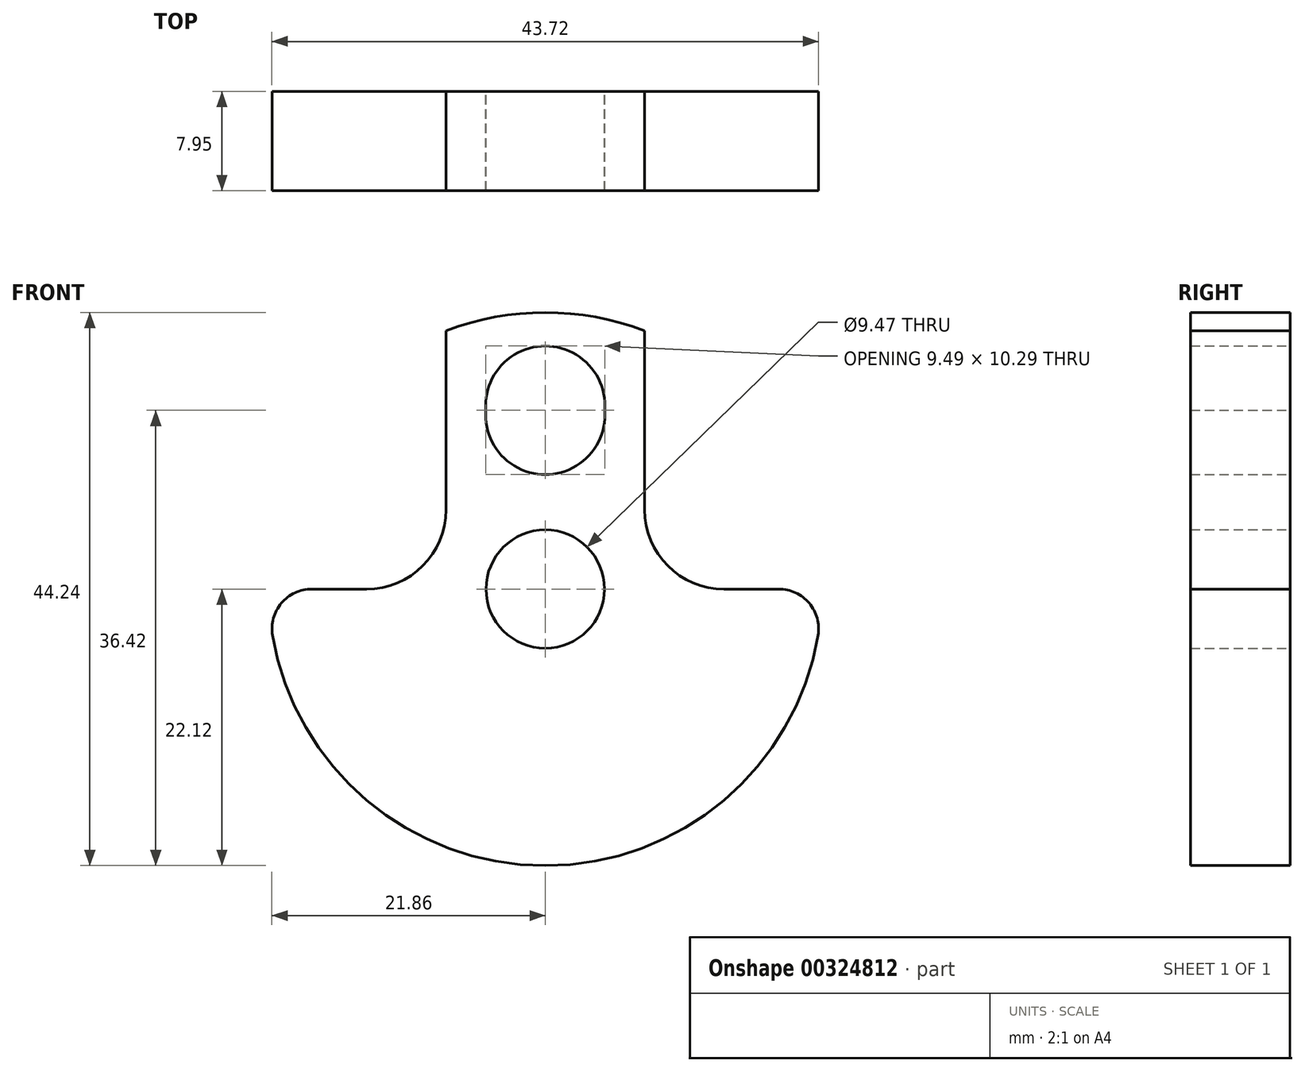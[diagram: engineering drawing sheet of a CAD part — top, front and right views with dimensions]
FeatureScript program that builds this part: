
annotation { "Feature Type Name" : "Feature", "Feature Type Description" : "" }
export const myFeature = defineFeature(function(context is Context, id is Id, definition is map)
    precondition{}
    {
        {
            var Q0;
            Q0=qCreatedBy(makeId("Front.planeOp"),FACE);
            var sketch = newSketch(context, id + "F0", { "sketchPlane" : qUnion([Q0])});
            skArc(sketch, "E0", {"start": v(-22.12, 0) * mm, "mid": v(0, -22.12) * mm, "end": v(22.12, 0) * mm});
            skCircle(sketch, "E1", {"center": v(0, 0) * mm, "radius": 4.74 * mm});
            skLineSegment(sketch, "E2", {"start": v(-7.94, 0) * mm, "end": v(-7.94, 20.65) * mm});
            skLineSegment(sketch, "E3.MirrorCS", {"start": v(7.94, 0) * mm, "end": v(7.94, 20.65) * mm});
            skLineSegment(sketch, "E4", {"start": v(-7.94, 0) * mm, "end": v(-22.12, 0) * mm});
            skLineSegment(sketch, "E5", {"start": v(7.94, 0) * mm, "end": v(22.12, 0) * mm});
            skArc(sketch, "E6", {"start": v(4.75, 14.3) * mm, "mid": v(0, 19.44) * mm, "end": v(-4.75, 14.3) * mm});
            skArc(sketch, "E7", {"start": v(-4.75, 14.3) * mm, "mid": v(0, 9.16) * mm, "end": v(4.75, 14.3) * mm});
            skArc(sketch, "E8.trimOffspring", {"start": v(7.94, 20.65) * mm, "mid": v(0, 22.12) * mm, "end": v(-7.94, 20.65) * mm});
            skSolve(sketch);
        }
        {
            var Q0;
            Q0=makeQuery(id+"F0.imprint","IMPRINT",FACE,{"disambiguationData":[TD([[makeQuery(id+"F0.imprint","IMPRINT",EDGE,{"derivedFrom":sQuery(id+"F0.wireOp",EDGE,"E0")}),1.0]])]});
            extrude(context, id + "F1", {"entities" : qUnion([Q0]), "depth" : 7.95 * mm, "offsetDistance" : 25.4 * mm});
        }
        {
            var Q0;
            Q0=makeQuery(id+"F1.opExtrude","SWEPT_EDGE",EDGE,{"disambiguationData":[OSD([sQuery(id+"F0.wireOp",EDGE,"E2"),sQuery(id+"F0.wireOp",EDGE,"E4")])]});
            var Q1;
            Q1=makeQuery(id+"F1.opExtrude","SWEPT_EDGE",EDGE,{"disambiguationData":[OSD([sQuery(id+"F0.wireOp",EDGE,"E3.MirrorCS"),sQuery(id+"F0.wireOp",EDGE,"E5")])]});
            fillet(context, id + "F2", {"entities" : qUnion([Q0, Q1]), "radius" : 6.35 * mm, "tangentPropagation" : true, "allowEdgeOverflow" : false});
        }
        {
            var Q0;
            Q0=makeQuery(id+"F1.opExtrude","SWEPT_EDGE",EDGE,{"disambiguationData":[OSD([sQuery(id+"F0.wireOp",EDGE,"E0"),sQuery(id+"F0.wireOp",EDGE,"E5")])]});
            var Q1;
            Q1=makeQuery(id+"F1.opExtrude","SWEPT_EDGE",EDGE,{"disambiguationData":[OSD([sQuery(id+"F0.wireOp",EDGE,"E0"),sQuery(id+"F0.wireOp",EDGE,"E4")])]});
            fillet(context, id + "F3", {"entities" : qUnion([Q0, Q1]), "radius" : 3.17 * mm, "tangentPropagation" : true, "allowEdgeOverflow" : false});
        }
    });
